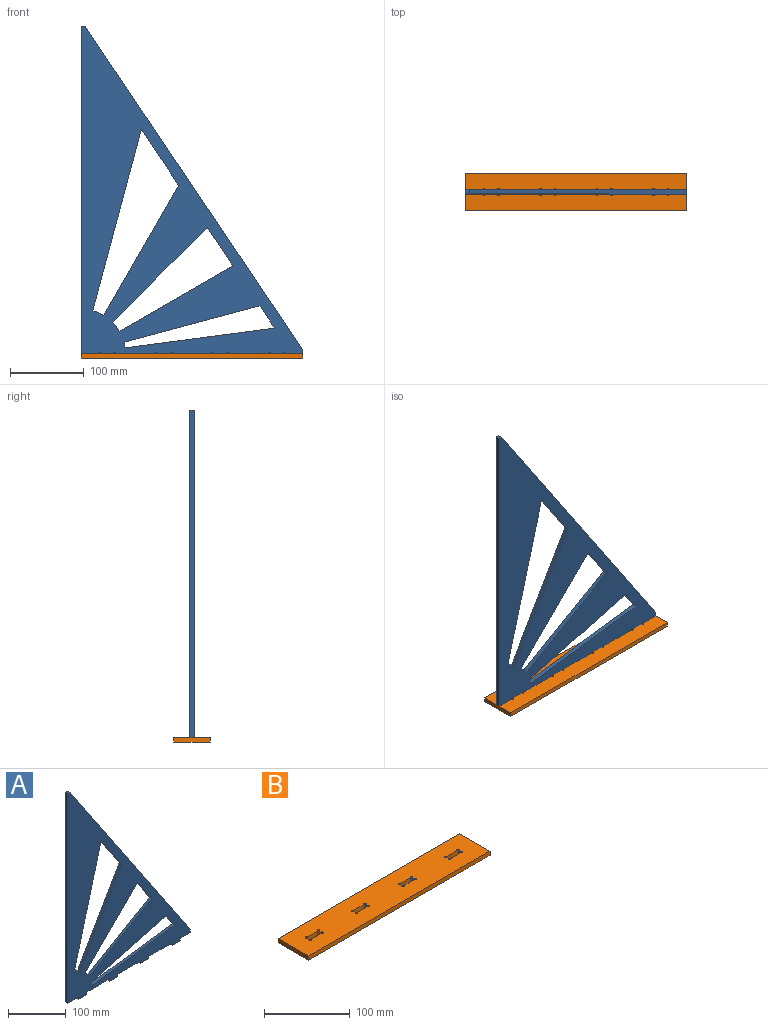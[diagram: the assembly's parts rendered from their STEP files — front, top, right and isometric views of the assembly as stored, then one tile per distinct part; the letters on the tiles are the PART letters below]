
ASSEMBLY  parts=2 mates=1
PART A: 43 faces, bbox 300x6x449 mm
  f0: plane 183.8x49.25mm, normal (0.26,0,-0.97), area 1141.7mm2, adj f1,f40,f41,f42
  f1: plane 30.27x20.34mm, normal (-0.83,0,-0.56), area 218.8mm2, adj f0,f2,f41,f42
  f2: plane 202.61x26.67mm, normal (-0.13,0,0.99), area 1226.2mm2, adj f1,f40,f41,f42
  f3: plane 153.58x88.67mm, normal (-0.5,0,0.87), area 1064mm2, adj f4,f37,f41,f42
  f4: cylinder r=60mm len=12.43mm, axis (0,1,0), area 94.2mm2, adj f3,f5,f41,f42
  f5: plane 128.2x128.2mm, normal (0.71,0,-0.71), area 1087.8mm2, adj f4,f37,f41,f42
  f6: plane 176.39x101.84mm, normal (-0.87,0,0.5), area 1222.1mm2, adj f7,f38,f41,f42
  f7: cylinder r=60mm len=14.47mm, axis (0,1,0), area 94.2mm2, adj f6,f8,f41,f42
  f8: plane 245.56x65.8mm, normal (0.97,0,-0.26), area 1525.4mm2, adj f7,f38,f41,f42
  f9: plane 23.5x6mm, normal (0,0,-1), area 141mm2, adj f10,f39,f41,f42
  f10: plane 6x5mm, normal (1,0,0), area 30mm2, adj f9,f11,f41,f42
  f11: plane 439x295mm, normal (0.83,0,0.56), area 3173.5mm2, adj f10,f12,f41,f42
  f12: plane 6x5mm, normal (0,0,1), area 30mm2, adj f11,f13,f41,f42
  f13: plane 444x6mm, normal (-1,0,0), area 2664mm2, adj f12,f14,f41,f42
  f14: plane 23.5x6mm, normal (0,0,-1), area 141mm2, adj f13,f15,f41,f42
  f15: cylinder r=1.5mm len=6mm, axis (0,1,0), area 42.4mm2, adj f14,f16,f41,f42
  f16: plane 6x3.5mm, normal (-1,0,0), area 21mm2, adj f15,f17,f41,f42
  f17: plane 20x6mm, normal (0,0,-1), area 120mm2, adj f16,f18,f41,f42
  f18: plane 6x3.5mm, normal (1,0,0), area 21mm2, adj f17,f19,f41,f42
  f19: cylinder r=1.5mm len=6mm, axis (0,1,0), area 42.4mm2, adj f18,f20,f41,f42
  f20: plane 53.67x6mm, normal (0,0,-1), area 322mm2, adj f19,f21,f41,f42
  f21: cylinder r=1.5mm len=6mm, axis (0,1,0), area 42.4mm2, adj f20,f22,f41,f42
  f22: plane 6x3.5mm, normal (-1,0,0), area 21mm2, adj f21,f23,f41,f42
  f23: plane 20x6mm, normal (0,0,-1), area 120mm2, adj f22,f24,f41,f42
  f24: plane 6x3.5mm, normal (1,0,0), area 21mm2, adj f23,f25,f41,f42
  f25: cylinder r=1.5mm len=6mm, axis (0,1,0), area 42.4mm2, adj f24,f26,f41,f42
  f26: plane 53.67x6mm, normal (0,0,-1), area 322mm2, adj f25,f27,f41,f42
  f27: cylinder r=1.5mm len=6mm, axis (0,1,0), area 42.4mm2, adj f26,f28,f41,f42
  f28: plane 6x3.5mm, normal (-1,0,0), area 21mm2, adj f27,f29,f41,f42
  f29: plane 20x6mm, normal (0,0,-1), area 120mm2, adj f28,f30,f41,f42
  f30: plane 6x3.5mm, normal (1,0,0), area 21mm2, adj f29,f31,f41,f42
  f31: cylinder r=1.5mm len=6mm, axis (0,1,0), area 42.4mm2, adj f30,f32,f41,f42
  f32: plane 53.67x6mm, normal (0,0,-1), area 322mm2, adj f31,f33,f41,f42
  f33: cylinder r=1.5mm len=6mm, axis (0,1,0), area 42.4mm2, adj f32,f34,f41,f42
  f34: plane 6x3.5mm, normal (-1,0,0), area 21mm2, adj f33,f35,f41,f42
  f35: plane 20x6mm, normal (0,0,-1), area 120mm2, adj f34,f36,f41,f42
  f36: plane 6x3.5mm, normal (1,0,0), area 21mm2, adj f35,f39,f41,f42
  f37: plane 51.96x34.92mm, normal (-0.83,0,-0.56), area 375.6mm2, adj f3,f5,f41,f42
  f38: plane 75.17x50.51mm, normal (-0.83,0,-0.56), area 543.4mm2, adj f6,f8,f41,f42
  f39: cylinder r=1.5mm len=6mm, axis (0,1,0), area 42.4mm2, adj f9,f36,f41,f42
  f40: cylinder r=60mm len=7.7mm, axis (0,1,0), area 47.1mm2, adj f0,f2,f41,f42
  f41: plane 449x300mm, normal (0,-1,0), area 47531.3mm2, adj f0,f1,f2,f3,f4,f5,f6,f7
  f42: plane 449x300mm, normal (0,1,0), area 47531.3mm2, adj f0,f1,f2,f3,f4,f5,f6,f7
PART B: 38 faces, bbox 300x50x6 mm
  f0: plane 300x50mm, normal (0,0,-1), area 14435.2mm2, adj f1,f2,f3,f4,f5,f6,f7,f8
  f1: plane 17x6mm, normal (0,-1,0), area 102mm2, adj f0,f21,f31,f33
  f2: plane 6x3mm, normal (-1,0,0), area 18mm2, adj f0,f21,f31,f32
  f3: plane 17x6mm, normal (0,1,0), area 102mm2, adj f0,f21,f22,f32
  f4: plane 17x6mm, normal (0,-1,0), area 102mm2, adj f0,f21,f34,f35
  f5: plane 6x3mm, normal (-1,0,0), area 18mm2, adj f0,f21,f35,f36
  f6: plane 17x6mm, normal (0,1,0), area 102mm2, adj f0,f21,f30,f36
  f7: plane 17x6mm, normal (0,-1,0), area 102mm2, adj f0,f21,f23,f24
  f8: plane 6x3mm, normal (-1,0,0), area 18mm2, adj f0,f21,f24,f25
  f9: plane 17x6mm, normal (0,1,0), area 102mm2, adj f0,f21,f25,f37
  f10: plane 17x6mm, normal (0,-1,0), area 102mm2, adj f0,f21,f27,f28
  f11: plane 6x3mm, normal (-1,0,0), area 18mm2, adj f0,f21,f28,f29
  f12: plane 17x6mm, normal (0,1,0), area 102mm2, adj f0,f21,f26,f29
  f13: plane 50x6mm, normal (1,0,0), area 300mm2, adj f0,f14,f19,f21
  f14: plane 300x6mm, normal (0,1,0), area 1800mm2, adj f0,f13,f15,f21
  f15: plane 50x6mm, normal (-1,0,0), area 300mm2, adj f0,f14,f19,f21
  f16: plane 6x3mm, normal (1,0,0), area 18mm2, adj f0,f21,f30,f34
  f17: plane 6x3mm, normal (1,0,0), area 18mm2, adj f0,f21,f23,f37
  f18: plane 6x3mm, normal (1,0,0), area 18mm2, adj f0,f21,f26,f27
  f19: plane 300x6mm, normal (0,-1,0), area 1800mm2, adj f0,f13,f15,f21
  f20: plane 6x3mm, normal (1,0,0), area 18mm2, adj f0,f21,f22,f33
  f21: plane 300x50mm, normal (0,0,1), area 14435.2mm2, adj f1,f2,f3,f4,f5,f6,f7,f8
  f22: cylinder r=1.5mm len=6mm, axis (0,0,-1), area 42.4mm2, adj f0,f3,f20,f21
  f23: cylinder r=1.5mm len=6mm, axis (0,0,-1), area 42.4mm2, adj f0,f7,f17,f21
  f24: cylinder r=1.5mm len=6mm, axis (0,0,-1), area 42.4mm2, adj f0,f7,f8,f21
  f25: cylinder r=1.5mm len=6mm, axis (0,0,-1), area 42.4mm2, adj f0,f8,f9,f21
  f26: cylinder r=1.5mm len=6mm, axis (0,0,-1), area 42.4mm2, adj f0,f12,f18,f21
  f27: cylinder r=1.5mm len=6mm, axis (0,0,-1), area 42.4mm2, adj f0,f10,f18,f21
  f28: cylinder r=1.5mm len=6mm, axis (0,0,-1), area 42.4mm2, adj f0,f10,f11,f21
  f29: cylinder r=1.5mm len=6mm, axis (0,0,-1), area 42.4mm2, adj f0,f11,f12,f21
  f30: cylinder r=1.5mm len=6mm, axis (0,0,-1), area 42.4mm2, adj f0,f6,f16,f21
  f31: cylinder r=1.5mm len=6mm, axis (0,0,-1), area 42.4mm2, adj f0,f1,f2,f21
  f32: cylinder r=1.5mm len=6mm, axis (0,0,-1), area 42.4mm2, adj f0,f2,f3,f21
  f33: cylinder r=1.5mm len=6mm, axis (0,0,-1), area 42.4mm2, adj f0,f1,f20,f21
  f34: cylinder r=1.5mm len=6mm, axis (0,0,-1), area 42.4mm2, adj f0,f4,f16,f21
  f35: cylinder r=1.5mm len=6mm, axis (0,0,-1), area 42.4mm2, adj f0,f4,f5,f21
  f36: cylinder r=1.5mm len=6mm, axis (0,0,-1), area 42.4mm2, adj f0,f5,f6,f21
  f37: cylinder r=1.5mm len=6mm, axis (0,0,-1), area 42.4mm2, adj f0,f9,f17,f21
PLACE A t=(115.49,17.16,-220.73)mm
PLACE B t=(-37.87,14.16,-226.73)mm
MATE fastened A.f10 <-> B.f13  axis (1,0,0) through (112.13,14.16,-220.73)mm
